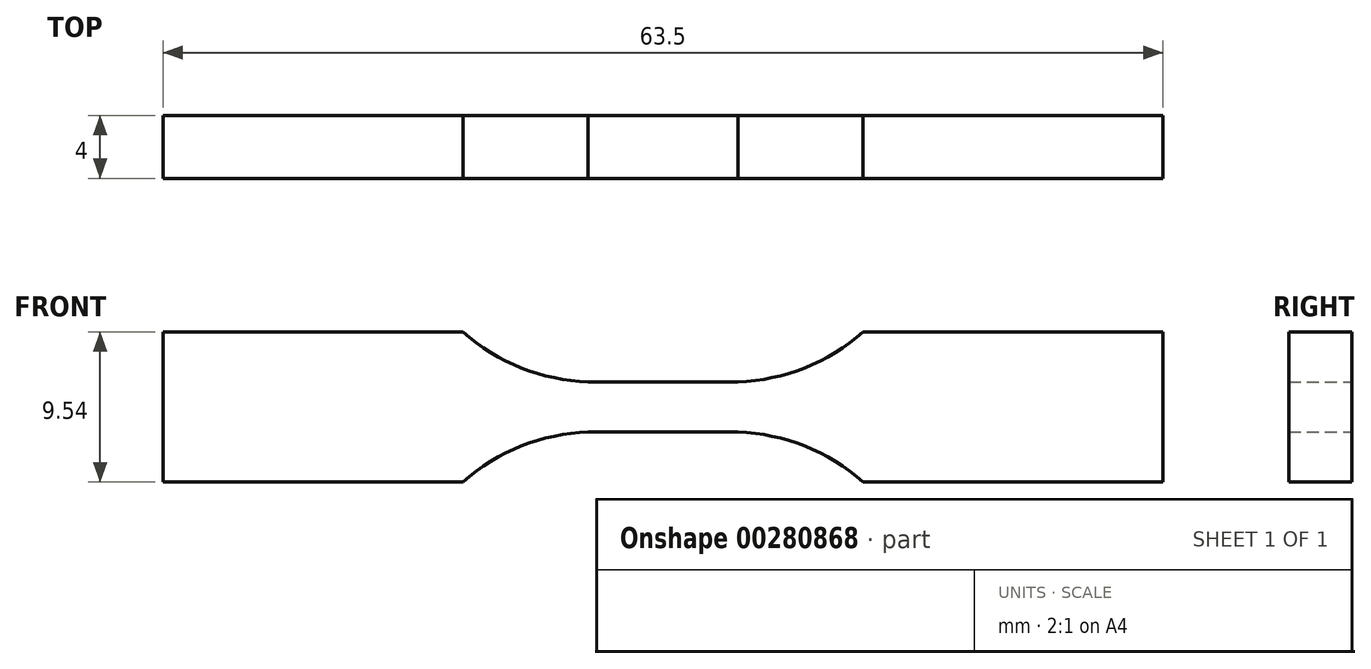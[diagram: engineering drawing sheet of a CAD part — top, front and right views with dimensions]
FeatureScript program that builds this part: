
annotation { "Feature Type Name" : "Feature", "Feature Type Description" : "" }
export const myFeature = defineFeature(function(context is Context, id is Id, definition is map)
    precondition{}
    {
        {
            var Q0;
            Q0=qCreatedBy(makeId("Front.planeOp"),FACE);
            var sketch = newSketch(context, id + "F0", { "sketchPlane" : qUnion([Q0])});
            skLineSegment(sketch, "E0", {"start": v(0, 1.59) * mm, "end": v(4.76, 1.59) * mm});
            skArc(sketch, "E1", {"start": v(4.77, 1.6) * mm, "mid": v(9, 2.49) * mm, "end": v(12.7, 4.77) * mm});
            skLineSegment(sketch, "E2", {"start": v(12.7, 4.76) * mm, "end": v(31.75, 4.76) * mm});
            skLineSegment(sketch, "E3.MirrorCS", {"start": v(12.7, -4.76) * mm, "end": v(31.75, -4.76) * mm});
            skLineSegment(sketch, "E4.MirrorCS", {"start": v(0, -1.6) * mm, "end": v(4.77, -1.6) * mm});
            skArc(sketch, "E5.MirrorCS", {"start": v(4.77, -1.6) * mm, "mid": v(9, -2.49) * mm, "end": v(12.7, -4.77) * mm});
            skLineSegment(sketch, "E6.MirrorCS", {"start": v(12.7, -4.77) * mm, "end": v(31.75, -4.77) * mm});
            skLineSegment(sketch, "E7.MirrorCS", {"start": v(0, 1.6) * mm, "end": v(-4.76, 1.6) * mm});
            skArc(sketch, "E8.MirrorCS", {"start": v(-4.77, 1.6) * mm, "mid": v(-9, 2.49) * mm, "end": v(-12.7, 4.77) * mm});
            skLineSegment(sketch, "E9.MirrorCS", {"start": v(-12.7, 4.76) * mm, "end": v(-31.75, 4.76) * mm});
            skLineSegment(sketch, "E10.MirrorCS", {"start": v(-12.7, -4.77) * mm, "end": v(-31.75, -4.77) * mm});
            skArc(sketch, "E11.MirrorCS", {"start": v(-4.77, -1.6) * mm, "mid": v(-9, -2.49) * mm, "end": v(-12.7, -4.77) * mm});
            skLineSegment(sketch, "E12.MirrorCS", {"start": v(0, -1.59) * mm, "end": v(-4.77, -1.59) * mm});
            skLineSegment(sketch, "E13.MirrorCS", {"start": v(0, -1.59) * mm, "end": v(-4.76, -1.59) * mm});
            skLineSegment(sketch, "E14", {"start": v(-31.75, 4.77) * mm, "end": v(-31.75, -4.77) * mm});
            skLineSegment(sketch, "E15", {"start": v(31.75, -4.76) * mm, "end": v(31.75, 4.77) * mm});
            skSolve(sketch);
        }
        {
            var Q0;
            Q0=makeQuery(id+"F0.imprint","IMPRINT",FACE,{"disambiguationData":[TD([[makeQuery(id+"F0.imprint","IMPRINT",EDGE,{"derivedFrom":sQuery(id+"F0.wireOp",EDGE,"E1")}),-1.0]])]});
            extrude(context, id + "F1", {"entities" : qUnion([Q0]), "endBound" : BoundingType.SYMMETRIC, "depth" : 4 * mm});
        }
    });
